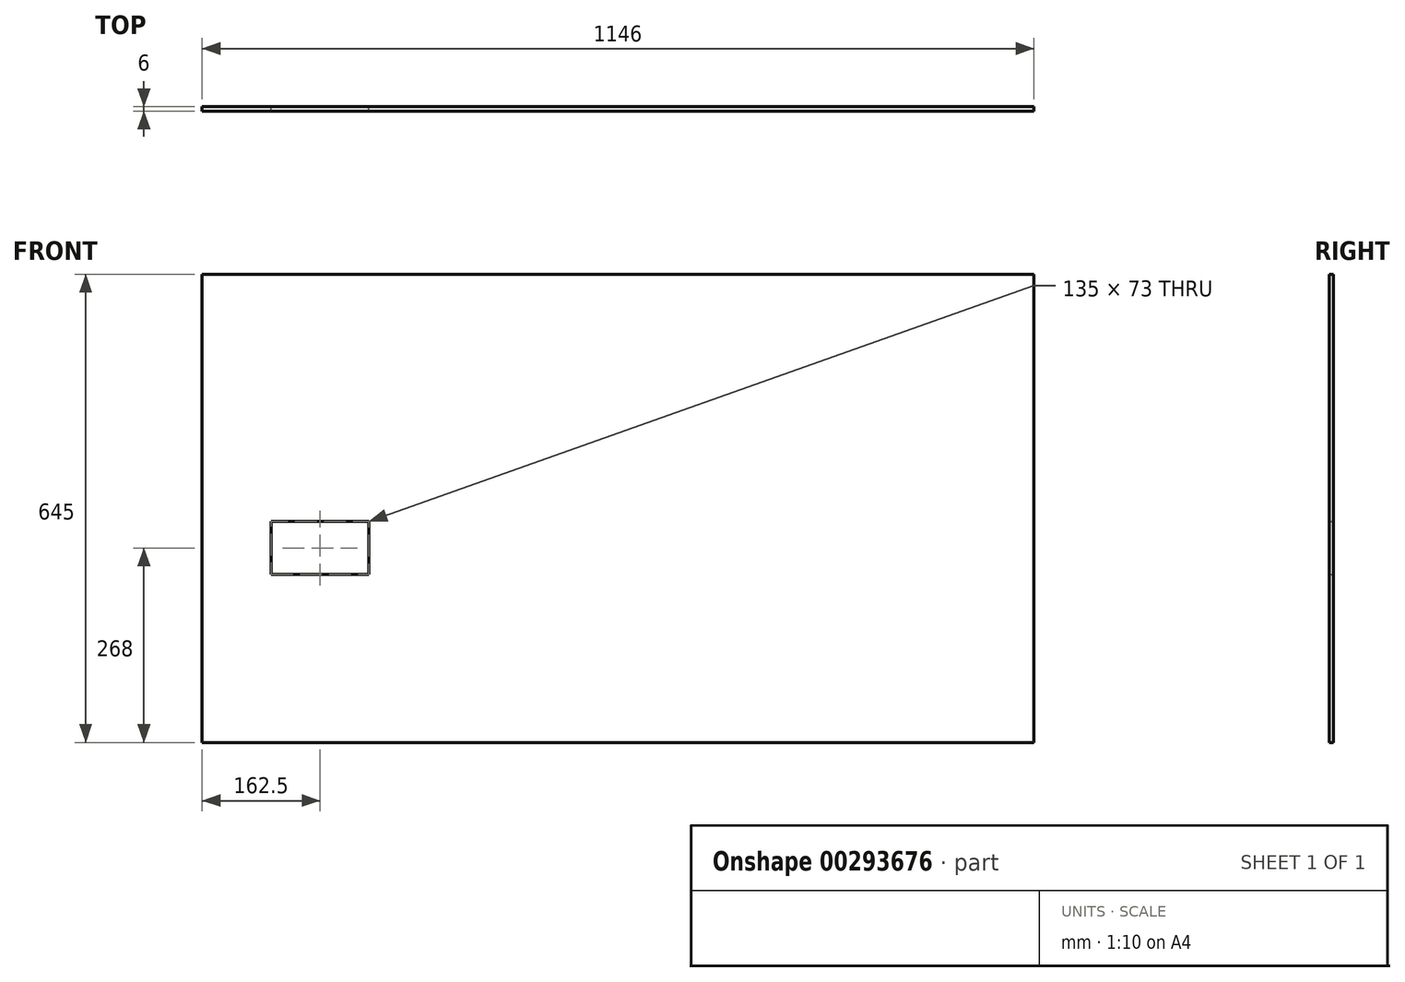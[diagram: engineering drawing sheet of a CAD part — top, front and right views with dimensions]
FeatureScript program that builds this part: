
annotation { "Feature Type Name" : "Feature", "Feature Type Description" : "" }
export const myFeature = defineFeature(function(context is Context, id is Id, definition is map)
    precondition{}
    {
        {
            var Q0;
            Q0=qCreatedBy(makeId("Front.planeOp"),FACE);
            var sketch = newSketch(context, id + "F0", { "sketchPlane" : qUnion([Q0])});
            skLineSegment(sketch, "E0.bottom", {"start": v(-370, 227) * mm, "end": v(776, 227) * mm});
            skLineSegment(sketch, "E0.top", {"start": v(-370, -418) * mm, "end": v(776, -418) * mm});
            skLineSegment(sketch, "E0.left", {"start": v(-370, 227) * mm, "end": v(-370, -418) * mm});
            skLineSegment(sketch, "E0.right", {"start": v(776, 227) * mm, "end": v(776, -418) * mm});
            skLineSegment(sketch, "E1.bottom", {"start": v(-275, -113.5) * mm, "end": v(-140, -113.5) * mm});
            skLineSegment(sketch, "E1.top", {"start": v(-275, -186.5) * mm, "end": v(-140, -186.5) * mm});
            skLineSegment(sketch, "E1.left", {"start": v(-275, -113.5) * mm, "end": v(-275, -186.5) * mm});
            skLineSegment(sketch, "E1.right", {"start": v(-140, -113.5) * mm, "end": v(-140, -186.5) * mm});
            skLineSegment(sketch, "E2", {"start": v(-275, -150) * mm, "end": v(-140, -150) * mm, "construction": true});
            skLineSegment(sketch, "E3", {"start": v(-207.5, -186.5) * mm, "end": v(-207.5, -113.5) * mm, "construction": true});
            skSolve(sketch);
        }
        {
            var Q0;
            Q0=makeQuery(id+"F0.imprint","IMPRINT",FACE,{"disambiguationData":[TD([[makeQuery(id+"F0.imprint","IMPRINT",EDGE,{"derivedFrom":sQuery(id+"F0.wireOp",EDGE,"E0.bottom")}),-1.0]])]});
            extrude(context, id + "F1", {"entities" : qUnion([Q0]), "depth" : 6 * mm});
        }
    });
